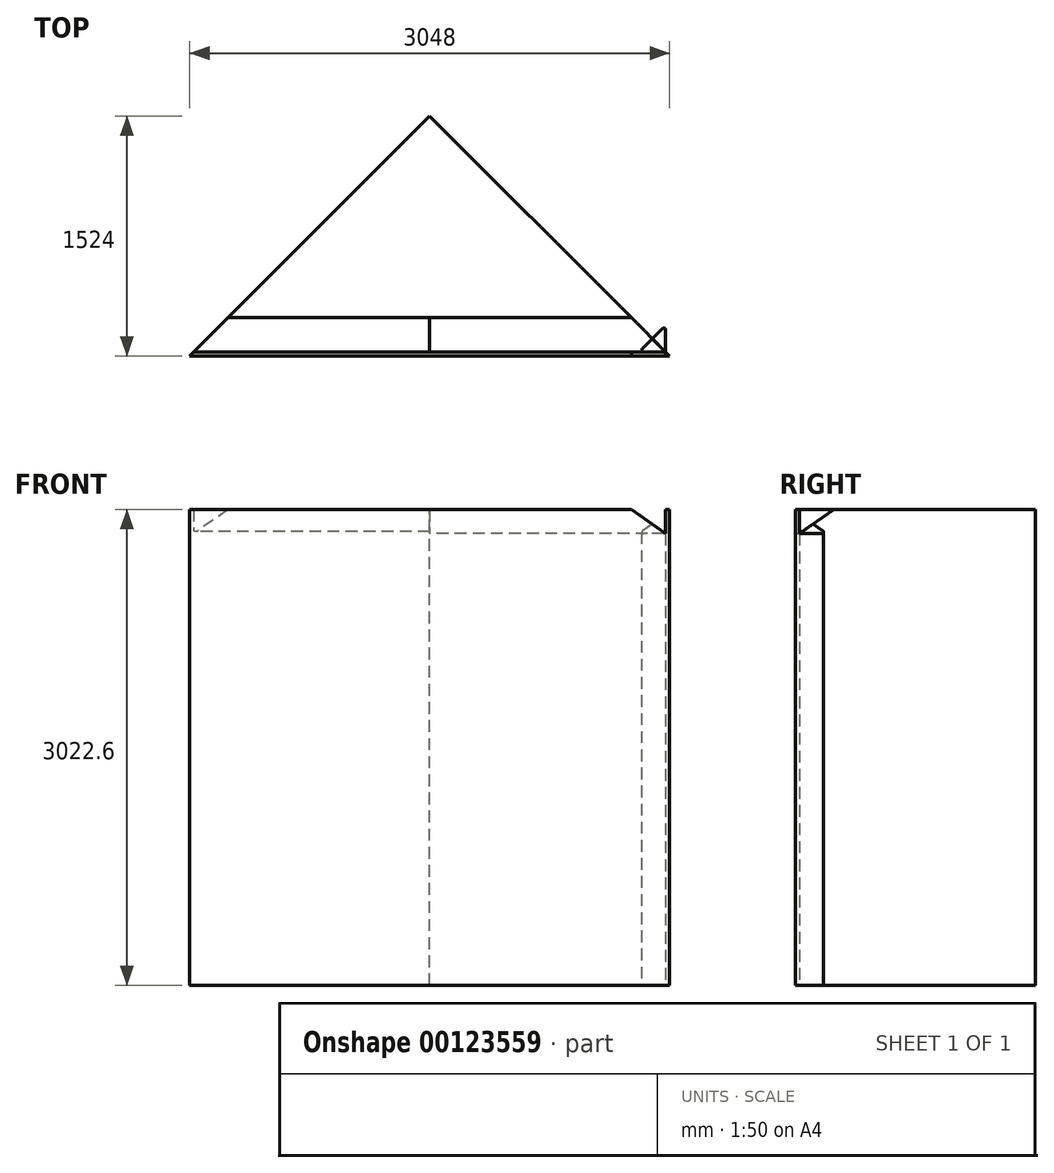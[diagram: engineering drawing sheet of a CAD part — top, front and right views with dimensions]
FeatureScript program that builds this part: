
annotation { "Feature Type Name" : "Feature", "Feature Type Description" : "" }
export const myFeature = defineFeature(function(context is Context, id is Id, definition is map)
    precondition{}
    {
        {
            var Q0;
            Q0=qCreatedBy(makeId("Top.planeOp"),FACE);
            var sketch = newSketch(context, id + "F0", { "sketchPlane" : qUnion([Q0])});
            skLineSegment(sketch, "E0.bottom", {"start": v(-1524, 1524) * mm, "end": v(1524, 1524) * mm});
            skLineSegment(sketch, "E0.top", {"start": v(-1524, -1524) * mm, "end": v(1524, -1524) * mm});
            skLineSegment(sketch, "E0.left", {"start": v(-1524, 1524) * mm, "end": v(-1524, -1524) * mm});
            skLineSegment(sketch, "E0.right", {"start": v(1524, 1524) * mm, "end": v(1524, -1524) * mm});
            skPoint(sketch, "E0.middle", {"position": v(0, 0) * mm});
            skSolve(sketch);
        }
        {
            var Q0;
            Q0 = qSketchRegion(id + "F0", true);
            extrude(context, id + "F1", {"entities" : qUnion([Q0]), "depth" : 3048 * mm});
        }
        {
            var Q0;
            Q0=qCreatedBy(makeId("Right.planeOp"),FACE);
            var sketch = newSketch(context, id + "F2", { "sketchPlane" : qUnion([Q0])});
            skLineSegment(sketch, "E1", {"start": v(-1498.6, 3022.6) * mm, "end": v(-1498.6, 2870.2) * mm});
            skLineSegment(sketch, "E2", {"start": v(-1498.6, 2870.2) * mm, "end": v(-1280.95, 3022.6) * mm});
            skLineSegment(sketch, "E3", {"start": v(-1280.95, 3022.6) * mm, "end": v(-1498.6, 3022.6) * mm});
            skSolve(sketch);
        }
        {
            var Q0;
            Q0 = qSketchRegion(id + "F2", true);
            extrude(context, id + "F3", {"entities" : qUnion([Q0]), "endBound" : BoundingType.SYMMETRIC, "depth" : 2997.2 * mm, "hasSecondDirection" : true, "secondDirectionOppositeDirection" : true, "secondDirectionDepth" : 25.4 * mm});
        }
        {
            var Q0;
            Q0=makeQuery(id+"F3.opExtrude","SWEPT_FACE",FACE,{"disambiguationData":[OSD([sQuery(id+"F2.wireOp",EDGE,"E3")])]});
            var sketch = newSketch(context, id + "F4", { "sketchPlane" : qUnion([Q0])});
            skLineSegment(sketch, "E4", {"start": v(0, 0) * mm, "end": v(1524, -1524) * mm});
            skLineSegment(sketch, "E5", {"start": v(0, 0) * mm, "end": v(-1524, -1524) * mm});
            skLineSegment(sketch, "E6", {"start": v(-1524, -1524) * mm, "end": v(1524, -1524) * mm});
            skSolve(sketch);
        }
        {
            var Q0;
            Q0 = qSketchRegion(id + "F4", true);
            extrude(context, id + "F5", {"entities" : qUnion([Q0]), "operationType" : NewBodyOperationType.INTERSECT, "endBound" : BoundingType.THROUGH_ALL, "oppositeDirection" : true, "depth" : 25.4 * mm});
        }
        {
            var Q0;
            Q0=makeQuery(id+"F3.opExtrude","SWEPT_EDGE",EDGE,{"disambiguationData":[OSD([sQuery(id+"F2.wireOp",EDGE,"E1"),sQuery(id+"F2.wireOp",EDGE,"E2")])]});
            fillet(context, id + "F6", {"entities" : qUnion([Q0]), "radius" : 12.7 * mm, "tangentPropagation" : true, "allowEdgeOverflow" : false});
        }
        {
            var Q0;
            Q0=qCreatedBy(makeId("Top.planeOp"),FACE);
            var sketch = newSketch(context, id + "F7", { "sketchPlane" : qUnion([Q0])});
            skLineSegment(sketch, "E7", {"start": v(1358.9, -1498.6) * mm, "end": v(1485.9, -1498.6) * mm});
            skLineSegment(sketch, "E8", {"start": v(1498.6, -1485.9) * mm, "end": v(1498.6, -1358.9) * mm});
            skLineSegment(sketch, "E9", {"start": v(1476.92, -1349.92) * mm, "end": v(1349.92, -1476.92) * mm});
            skPoint(sketch, "E10.visualSharp", {"position": v(1328.24, -1498.6) * mm});
            skArc(sketch, "E10.filletArc", {"start": v(1349.92, -1476.92) * mm, "mid": v(1347.17, -1490.76) * mm, "end": v(1358.9, -1498.6) * mm});
            skPoint(sketch, "E11.visualSharp", {"position": v(1498.6, -1328.24) * mm});
            skArc(sketch, "E11.filletArc", {"start": v(1498.6, -1358.9) * mm, "mid": v(1490.76, -1347.17) * mm, "end": v(1476.92, -1349.92) * mm});
            skPoint(sketch, "E12.visualSharp", {"position": v(1498.6, -1498.6) * mm});
            skArc(sketch, "E12.filletArc", {"start": v(1485.9, -1498.6) * mm, "mid": v(1494.88, -1494.88) * mm, "end": v(1498.6, -1485.9) * mm});
            skSolve(sketch);
        }
        {
            var Q0;
            Q0 = qSketchRegion(id + "F7", true);
            extrude(context, id + "F8", {"entities" : qUnion([Q0]), "depth" : 3022.6 * mm});
        }
        {
            var Q0;
            Q0=qCreatedBy(makeId("Front.planeOp"),FACE);
            var sketch = newSketch(context, id + "F9", { "sketchPlane" : qUnion([Q0])});
            skLineSegment(sketch, "E13", {"start": v(1498.6, 3022.6) * mm, "end": v(1498.6, 2870.2) * mm});
            skLineSegment(sketch, "E14", {"start": v(1498.6, 2870.2) * mm, "end": v(1280.95, 3022.6) * mm});
            skLineSegment(sketch, "E15", {"start": v(1498.6, 3022.6) * mm, "end": v(1280.95, 3022.6) * mm});
            skSolve(sketch);
        }
        {
            var Q0;
            Q0 = qSketchRegion(id + "F2", true);
            extrude(context, id + "F10", {"entities" : qUnion([Q0]), "operationType" : NewBodyOperationType.REMOVE, "endBound" : BoundingType.THROUGH_ALL, "depth" : 25.4 * mm});
        }
        {
            var Q0;
            Q0 = qSketchRegion(id + "F9", true);
            extrude(context, id + "F11", {"entities" : qUnion([Q0]), "operationType" : NewBodyOperationType.REMOVE, "endBound" : BoundingType.THROUGH_ALL, "depth" : 25.4 * mm});
        }
    });
